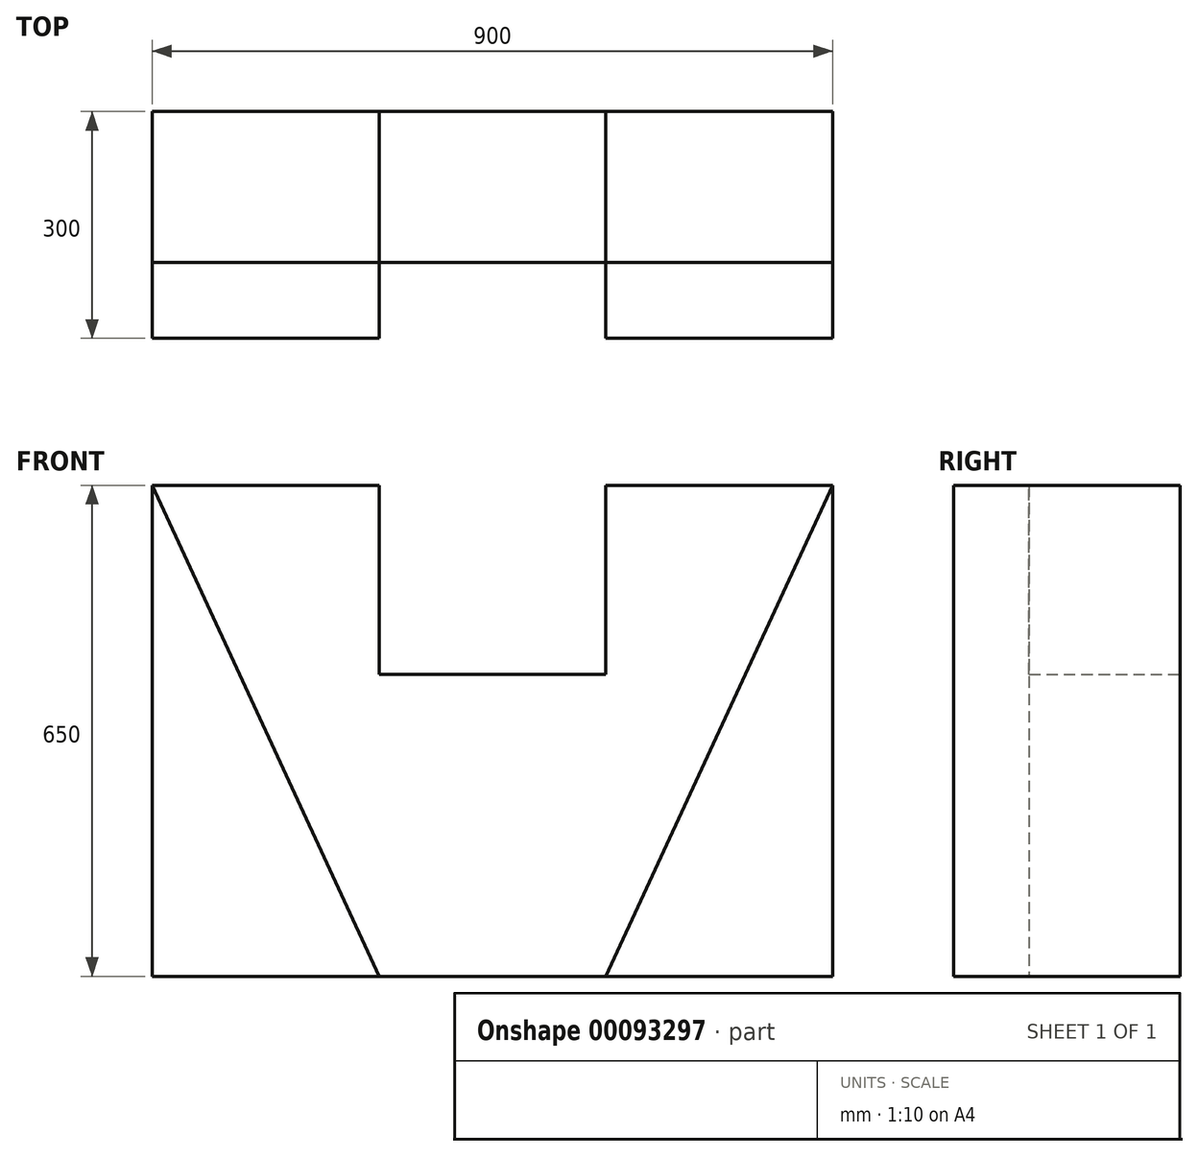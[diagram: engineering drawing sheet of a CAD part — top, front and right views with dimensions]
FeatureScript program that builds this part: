
annotation { "Feature Type Name" : "Feature", "Feature Type Description" : "" }
export const myFeature = defineFeature(function(context is Context, id is Id, definition is map)
    precondition{}
    {
        {
            var Q0;
            Q0=qCreatedBy(makeId("Front.planeOp"),FACE);
            var sketch = newSketch(context, id + "F0", { "sketchPlane" : qUnion([Q0])});
            skLineSegment(sketch, "E0.bottom", {"start": v(450, 325) * mm, "end": v(150, 325) * mm});
            skLineSegment(sketch, "E0.top", {"start": v(450, -325) * mm, "end": v(-450, -325) * mm});
            skLineSegment(sketch, "E0.left", {"start": v(450, 325) * mm, "end": v(450, -325) * mm});
            skLineSegment(sketch, "E0.right", {"start": v(-450, 325) * mm, "end": v(-450, -325) * mm});
            skPoint(sketch, "E0.middle", {"position": v(0, 0) * mm});
            skLineSegment(sketch, "E1.bottom", {"start": v(150, 75) * mm, "end": v(-150, 75) * mm});
            skLineSegment(sketch, "E1.left", {"start": v(150, 75) * mm, "end": v(150, 325) * mm});
            skLineSegment(sketch, "E1.right", {"start": v(-150, 75) * mm, "end": v(-150, 325) * mm});
            skPoint(sketch, "E1.middle", {"position": v(0, 325) * mm});
            skPoint(sketch, "E1.top.end.orphan", {"position": v(-150, 575) * mm});
            skPoint(sketch, "E2.orphan", {"position": v(150, 575) * mm});
            skLineSegment(sketch, "E3.trimOffspring", {"start": v(-150, 325) * mm, "end": v(-450, 325) * mm});
            skSolve(sketch);
        }
        {
            var Q0;
            Q0=makeQuery(id+"F0.imprint","IMPRINT",FACE,{"disambiguationData":[TD([[makeQuery(id+"F0.imprint","IMPRINT",EDGE,{"derivedFrom":sQuery(id+"F0.wireOp",EDGE,"E0.bottom")}),1.0]])]});
            extrude(context, id + "F1", {"entities" : qUnion([Q0]), "endBound" : BoundingType.SYMMETRIC, "depth" : 200 * mm});
        }
        {
            var Q0;
            Q0=makeQuery(id+"F1.opExtrude","CAP_FACE",FACE,{"disambiguationData":[OSD([sQuery(id+"F0.wireOp",EDGE,"E0.bottom"),sQuery(id+"F0.wireOp",EDGE,"E0.top"),sQuery(id+"F0.wireOp",EDGE,"E0.left"),sQuery(id+"F0.wireOp",EDGE,"E0.right"),sQuery(id+"F0.wireOp",EDGE,"E1.bottom"),sQuery(id+"F0.wireOp",EDGE,"E1.left"),sQuery(id+"F0.wireOp",EDGE,"E1.right"),sQuery(id+"F0.wireOp",EDGE,"E3.trimOffspring")])],"isStart":false});
            var sketch = newSketch(context, id + "F2", { "sketchPlane" : qUnion([Q0])});
            skLineSegment(sketch, "E4", {"start": v(-450, -325) * mm, "end": v(-150, -325) * mm});
            skLineSegment(sketch, "E5", {"start": v(-150, -325) * mm, "end": v(-450, 325) * mm});
            skLineSegment(sketch, "E6", {"start": v(-450, 325) * mm, "end": v(-450, -325) * mm});
            skLineSegment(sketch, "E7", {"start": v(450, -325) * mm, "end": v(150, -325) * mm});
            skLineSegment(sketch, "E8", {"start": v(150, -325) * mm, "end": v(450, 325) * mm});
            skLineSegment(sketch, "E9", {"start": v(450, 325) * mm, "end": v(450, -325) * mm});
            skSolve(sketch);
        }
        {
            var Q0;
            Q0=makeQuery(id+"F2.imprint","IMPRINT",FACE,{"disambiguationData":[TD([[makeQuery(id+"F2.imprint","IMPRINT",EDGE,{"derivedFrom":sQuery(id+"F2.wireOp",EDGE,"E4")}),-1.0]])]});
            var Q1;
            Q1=makeQuery(id+"F2.imprint","IMPRINT",FACE,{"disambiguationData":[TD([[makeQuery(id+"F2.imprint","IMPRINT",EDGE,{"derivedFrom":sQuery(id+"F2.wireOp",EDGE,"E7")}),-1.0]])]});
            extrude(context, id + "F3", {"entities" : qUnion([Q0, Q1]), "operationType" : NewBodyOperationType.ADD, "endBound" : BoundingType.SYMMETRIC, "depth" : 200 * mm});
        }
    });
